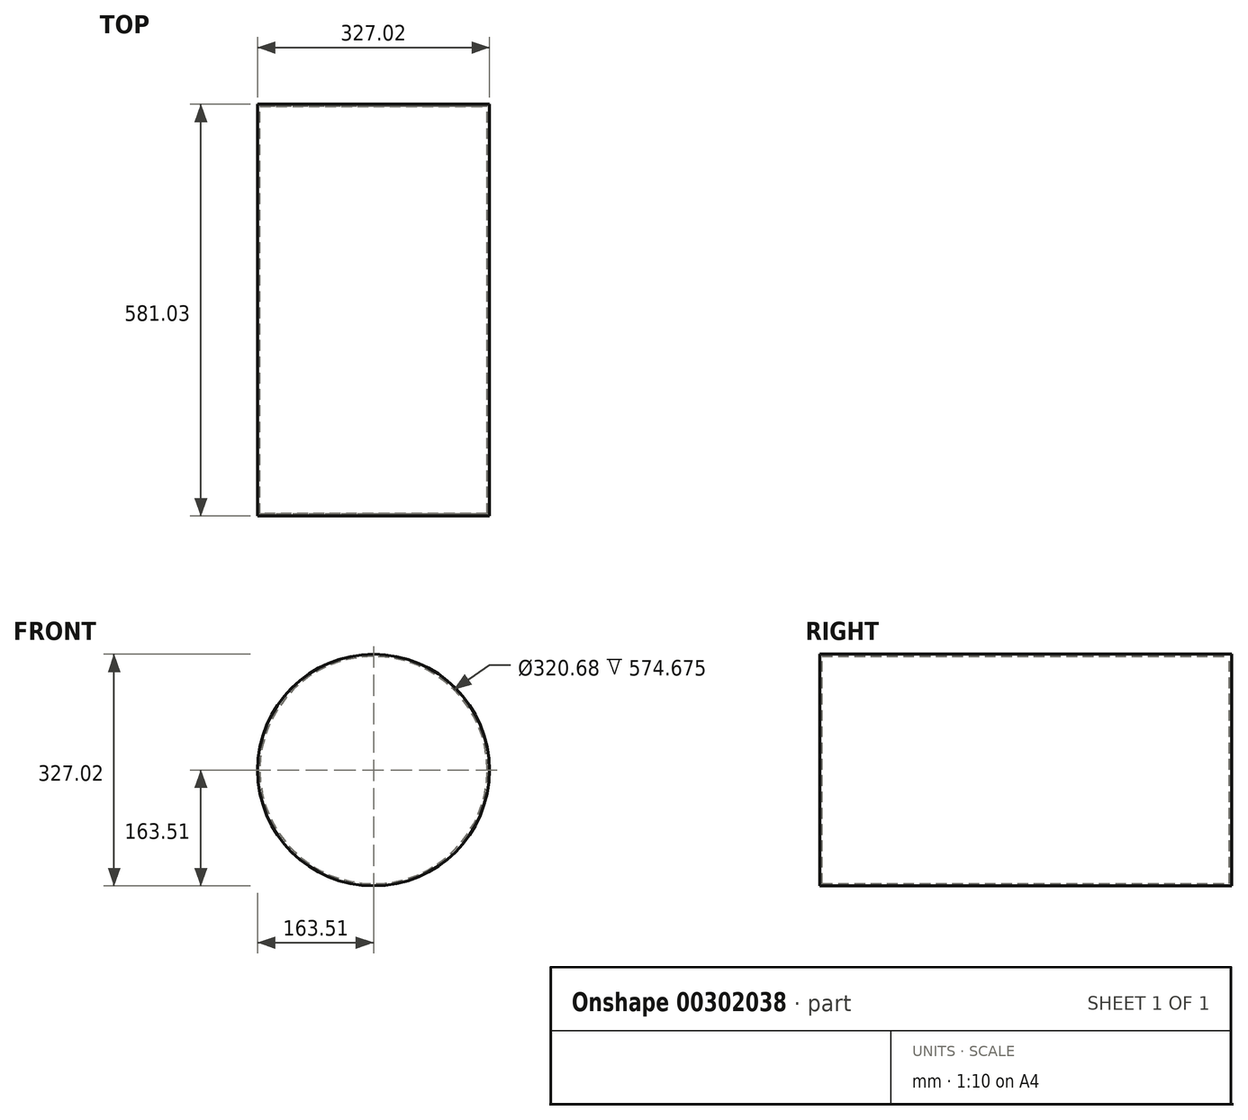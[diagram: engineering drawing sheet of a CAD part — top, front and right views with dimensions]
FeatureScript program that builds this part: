
annotation { "Feature Type Name" : "Feature", "Feature Type Description" : "" }
export const myFeature = defineFeature(function(context is Context, id is Id, definition is map)
    precondition{}
    {
        {
            var Q0;
            Q0=qCreatedBy(makeId("Front.planeOp"),FACE);
            var sketch = newSketch(context, id + "F0", { "sketchPlane" : qUnion([Q0])});
            skCircle(sketch, "E0", {"center": v(0, 0) * mm, "radius": 163.51 * mm});
            skCircle(sketch, "E1", {"center": v(0, 0) * mm, "radius": 160.34 * mm});
            skSolve(sketch);
        }
        {
            var Q0;
            Q0 = qSketchRegion(id + "F0", true);
            extrude(context, id + "F1", {"entities" : qUnion([Q0]), "depth" : 574.67 * mm});
        }
        {
            var Q0;
            Q0=makeQuery(id+"F1.opExtrude","CAP_FACE",FACE,{"disambiguationData":[OSD([sQuery(id+"F0.wireOp",EDGE,"E0"),sQuery(id+"F0.wireOp",EDGE,"E1")])],"isStart":false});
            var sketch = newSketch(context, id + "F2", { "sketchPlane" : qUnion([Q0])});
            skCircle(sketch, "E2", {"center": v(0, 0) * mm, "radius": 163.51 * mm});
            skSolve(sketch);
        }
        {
            var Q0;
            Q0 = qSketchRegion(id + "F2", true);
            extrude(context, id + "F3", {"entities" : qUnion([Q0]), "operationType" : NewBodyOperationType.ADD, "depth" : 3.17 * mm});
        }
        {
            var Q0;
            Q0=makeQuery(id+"F1.opExtrude","CAP_FACE",FACE,{"disambiguationData":[OSD([sQuery(id+"F0.wireOp",EDGE,"E0"),sQuery(id+"F0.wireOp",EDGE,"E1")])],"isStart":true});
            var sketch = newSketch(context, id + "F4", { "sketchPlane" : qUnion([Q0])});
            skCircle(sketch, "E3", {"center": v(0, 0) * mm, "radius": 163.51 * mm});
            skSolve(sketch);
        }
        {
            var Q0;
            Q0 = qSketchRegion(id + "F4", true);
            extrude(context, id + "F5", {"entities" : qUnion([Q0]), "operationType" : NewBodyOperationType.ADD, "depth" : 3.17 * mm});
        }
    });
